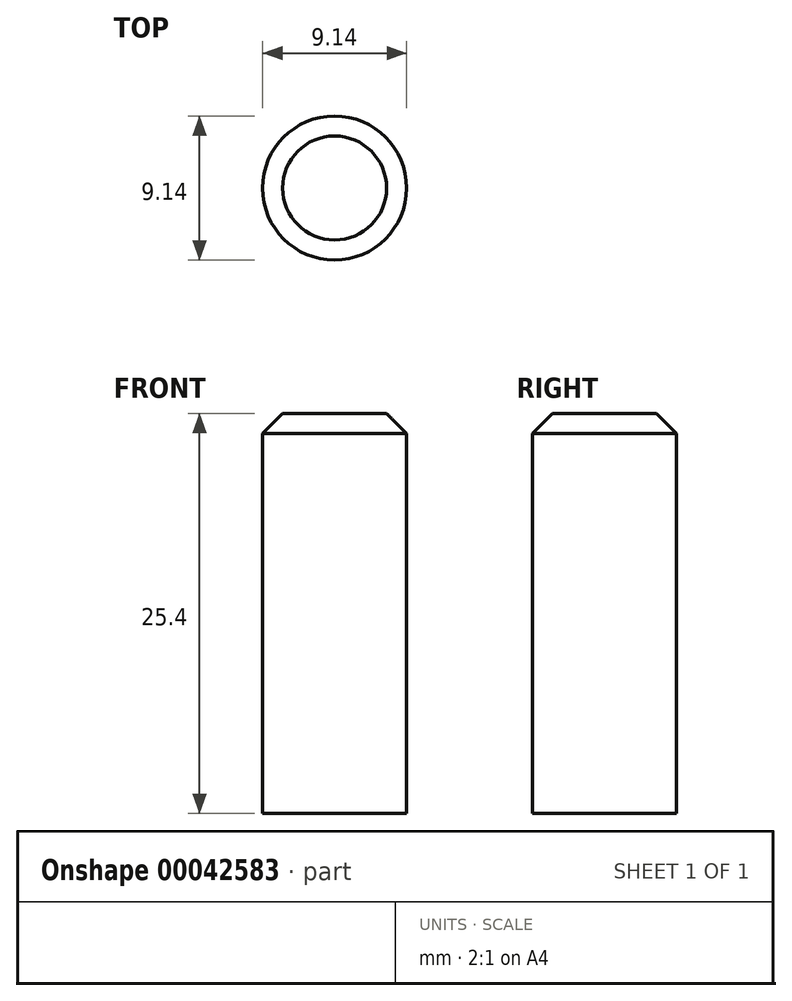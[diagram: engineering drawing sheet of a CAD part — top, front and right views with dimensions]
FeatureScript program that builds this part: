
annotation { "Feature Type Name" : "Feature", "Feature Type Description" : "" }
export const myFeature = defineFeature(function(context is Context, id is Id, definition is map)
    precondition{}
    {
        {
            var Q0;
            Q0=qCreatedBy(makeId("Top.planeOp"),FACE);
            var sketch = newSketch(context, id + "F0", { "sketchPlane" : qUnion([Q0])});
            skCircle(sketch, "E0", {"center": v(0, 0) * mm, "radius": 4.57 * mm});
            skSolve(sketch);
        }
        {
            var Q0;
            Q0 = qSketchRegion(id + "F0", true);
            extrude(context, id + "F1", {"entities" : qUnion([Q0]), "depth" : 25.4 * mm});
        }
        {
            var Q0;
            Q0=makeQuery(id+"F1.opExtrude","CAP_EDGE",EDGE,{"disambiguationData":[OSD([sQuery(id+"F0.wireOp",EDGE,"E0")])],"isStart":false});
            chamfer(context, id + "F2", {"entities" : qUnion([Q0]), "width" : 1.27 * mm, "tangentPropagation" : true});
        }
    });
